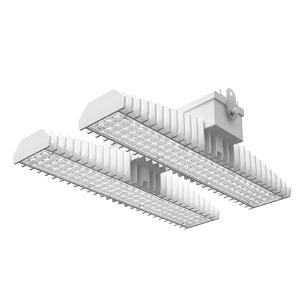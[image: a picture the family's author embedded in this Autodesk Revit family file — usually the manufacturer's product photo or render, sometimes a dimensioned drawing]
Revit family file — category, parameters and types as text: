
# Revit family: 3f_filippi_-_3f_lem_ht_ampio_3f_filippi_-_59026_a0812_-_3f_lem_2_ht_led_60_cr_ampio___vs_00af
name_source: partatom
category: Lighting Fixtures
units: mm (PartAtom-declared; Revit-internal decimal feet)

## family parameters
Cut with Voids When Loaded = No
Host = Face
Light Source = No
Part Type = Normal
Room Calculation Point = No
Round Connector Dimension = Use Diameter
Shared = No

## types (1)
- 3F Filippi - 3F LEM HT Ampio (1 x LED, 8518 lm, 68 W, 4000 K)
    Apparent Load = 68 VA
    Approval mark = ENEC
    CIE Flux Codes = 67 90 97 100 100
    Color Rendering = 80
    Color Temperature = 4000 K
    Control Gear = Electronic ballast
    Default Elevation = 1800 mm
    Description = Industrial luminaire with high light output and high luminous efficiency designed with the most innovative technologies for environments with temperature up to 70°C.

ILLUMINOTECHNICAL
Luminous efficiency 100% (DLOR 98%, ULOR 2%).
Initial luminous flux of the luminaire 8518 lm.
Direct symmetric wide distribution: the illuminated area has a rectangular shape.
Installation Interdistance Transv.D = 1.24 x hu - Long.D = 1.20 x hu.
Tabular UGR (CIE 117 - 4H-8H; S=0.25H; 70/50/20): RUG 20.6 - 20.6.
Beam angle: 82° - 83°.
Luminous efficacy 125 lm/W.
Lifetime (L93/B10): 30000 h. (tq+25°C)
Lifetime (L90/B10): 50000 h. (tq+25°C)
Lifetime (L85/B10): 80000 h. (tq+25°C)
Lifetime (L80/B10): 100000 h. (tq+25°C)
Lifetime (L85/B10): 50000 h. (tq+70°C)
Sudden decreased luminous flux after 50000 hours: 0% (C0).
Photobiological safety in compliance with IEC/TR 62778: RG0 risk exempt, (IEC 62471).
In compliance with IEC/EN 62722-2-1 - IEC/EN 62717 standards.
Luminous flux at +70°C: -13.5%.

SOURCE
2 Mid-Power linear LED modules 30W/840.
Energy efficiency class (UE 2019/2020 - UE 2019/2015): C.
CIE 13.3 Colour rendering index: CRI >80 (R9 <50%).
IES TM-30 Fidelity Index: Rf = 84 Rg = 95.
CCT nominal colour temperature 4000 K.
Colour initial tolerance (MacAdam): SDCM 3.

MECHANICAL
Passive modular heatsinks in die-casted aluminium, painted in white colour.
To optimize the thermal management of the LED module, the heatsinks are oversized and provided with self-cleaning of cooling fins.
Wiring body in aluminium and galvanised steel anchored solidly to the sinks and thermally separated.
3F Lens lenses with high luminous efficiency, transparent polycarbonate, fixed to the LED modules.
Fixing brackets in stainless steel.
Luminaire with limited surface temperature. - D - (EN 60598-2-24)
Dimensions: 470x542 mm, height 133 mm. Weight 9.965 kg.
IP65 protection degree.
Mechanical strength to impacts IK08 (5 joule).
Glow-wire test resistance 850°C.

ELECTRICAL
Halogen Free electronic wiring 230V-50/60Hz, power factor 0.95, THD <25%, constant output current, class I, 1 driver.
Power of the luminaire 68 W.
CE - IEC 60598-1 - EN 60598-1.
SAFE FLICKER: PstLM=<1 and SVM=<0.4 (IEC TR 61547-1 and IEC TR 63158), to ensure a more comfortable and safe light.
Luminaire compliant with EN 60598-2-22 for power supply from a centralised emergency system CPSS (Central Power Supply System), not incorporated in the luminaire - high risk areas excluded. The default power and flux are 100% in AC and 100% in DC.
Ambient temperature from -30°C to +70°C.
Temperature class T6 max 85°C.
Quick connection via M20 3P connector with 9-13 mm tightening range.
Power unit positioned on a separate compartment by the LED module to ensure optimum temperatures of cabling components, to be inspectable and maintainable.
Relative humidity UR: <85%.

INSTALLATION
Ceiling / Suspended / Wall.
All accessories dedicated to this product are available on the Catalog and on our website www.3F-Filippi.com.

ACCESSORIES
A0812 - Anti-glare microprismatic VS moulded glass, tempered, not flammable, with sealing gasket.
One required for each light module. The pack contains 10 pieces.

APPLICATIONS
In commercial environments, exhibition and industrial areas, stores, open areas.
Applications with high ambient temperature up to 70°C.

WARNING
Fixture not suitable for cold stores with an ambient temperature <0°C and/or relative humidity >85%.
Luminaire designed for disposal/recycling at end-of-life.
Replaceable (LED only) light source by a professional. Replaceable control gear by a professional.
    Height = 133 mm  [stored 0.436352 ft]
    Lamp = 1 x LED
    Lamp Light Flux = 8518 lm
    Lamp Power = 68 W
    Lamp count = 1
    Length = 470 mm
    Lifetime = 50000 h
    Luminous efficacy = 125 lm/W
    Manufacturer = 3F Filippi
    ModVariant = No
    Model = 3F Filippi - 59026+A0812 - 3F LEM 2 HT LED 60 CR AMPIO + VS
    Mounting Place = Ceiling
    Mounting Type = Pendant
    Number of Poles = 1
    OnlyDefault = Yes
    Power Factor = 1
    Product Name = 3F Filippi - 3F LEM HT Ampio
    Product group = pendant luminaire
    ProductGroupID = 9
    Protection Class = Protection class I
    Protection Degree = IP 65
    RLX_Detail_Level = 1
    RLX_Emergency_Light_Flux = 0 lm
    RLX_Emergency_Type = 0
    RLX_Emergency_Type_DB = No
    RlxData = <blob elided: 101237 chars, md5=9870b5b9>
    Socket = socket
    Standby Power = 0 W
    System Light Flux = 8518 lm
    System Power = 68 W
    Type Comments = Product without accessories
    Type Image = 3f_filippi_-_lem_2__a0811.jpg
    URL = http://relux.com
    VarID = ---
    Voltage = 0 V
    Weight = 0.00 kg
    Width = 542 mm

note: [stored X ft] marks values corroborated as IEEE doubles in the binary element streams (Revit-internal decimal feet)

## geometry (parser evidence)
native form markers: Blend x4, Sweep x12
no freeform markers — native parametric forms only
